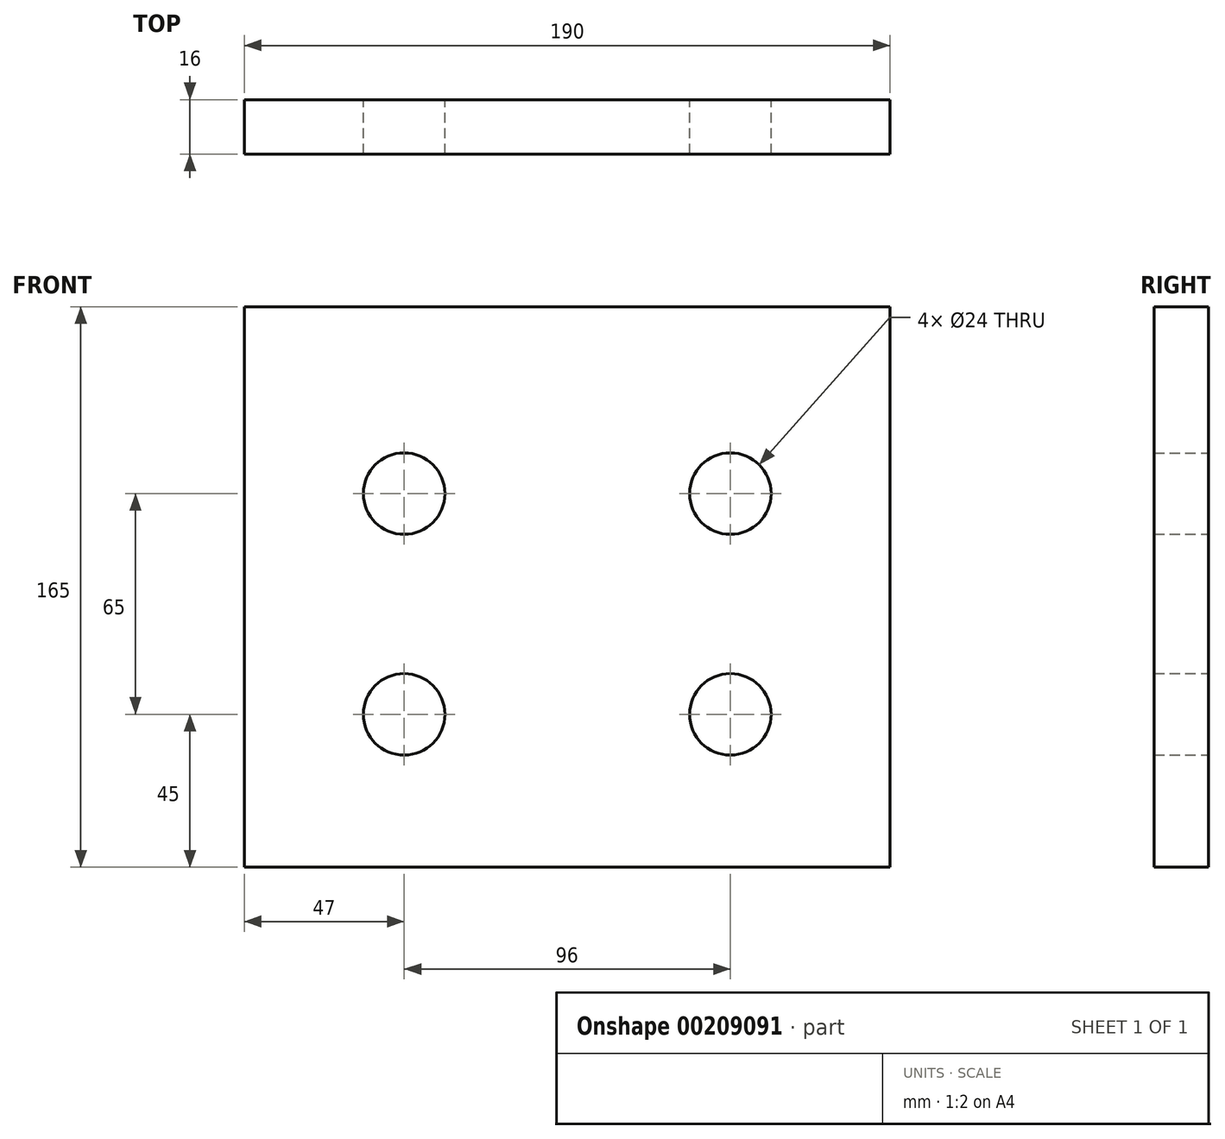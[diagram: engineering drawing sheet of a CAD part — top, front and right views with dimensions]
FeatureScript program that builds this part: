
annotation { "Feature Type Name" : "Feature", "Feature Type Description" : "" }
export const myFeature = defineFeature(function(context is Context, id is Id, definition is map)
    precondition{}
    {
        {
            var Q0;
            Q0=qCreatedBy(makeId("Front.planeOp"),FACE);
            var sketch = newSketch(context, id + "F0", { "sketchPlane" : qUnion([Q0])});
            skLineSegment(sketch, "E0.bottom", {"start": v(95, -82.5) * mm, "end": v(-95, -82.5) * mm});
            skLineSegment(sketch, "E0.top", {"start": v(95, 82.5) * mm, "end": v(-95, 82.5) * mm});
            skLineSegment(sketch, "E0.left", {"start": v(95, -82.5) * mm, "end": v(95, 82.5) * mm});
            skLineSegment(sketch, "E0.right", {"start": v(-95, -82.5) * mm, "end": v(-95, 82.5) * mm});
            skPoint(sketch, "E0.middle", {"position": v(0, 0) * mm});
            skCircle(sketch, "E1", {"center": v(-48, -37.5) * mm, "radius": 12 * mm});
            skCircle(sketch, "E2", {"center": v(-48, 27.5) * mm, "radius": 12 * mm});
            skCircle(sketch, "E3.MirrorC", {"center": v(48, 27.5) * mm, "radius": 12 * mm});
            skCircle(sketch, "E4.MirrorC", {"center": v(48, -37.5) * mm, "radius": 12 * mm});
            skSolve(sketch);
        }
        {
            var Q0;
            Q0=qSketchRegion(id+"F0",true);
            extrude(context, id + "F1", {"entities" : qUnion([Q0]), "depth" : 16 * mm, "symmetric" : true});
        }
    });
